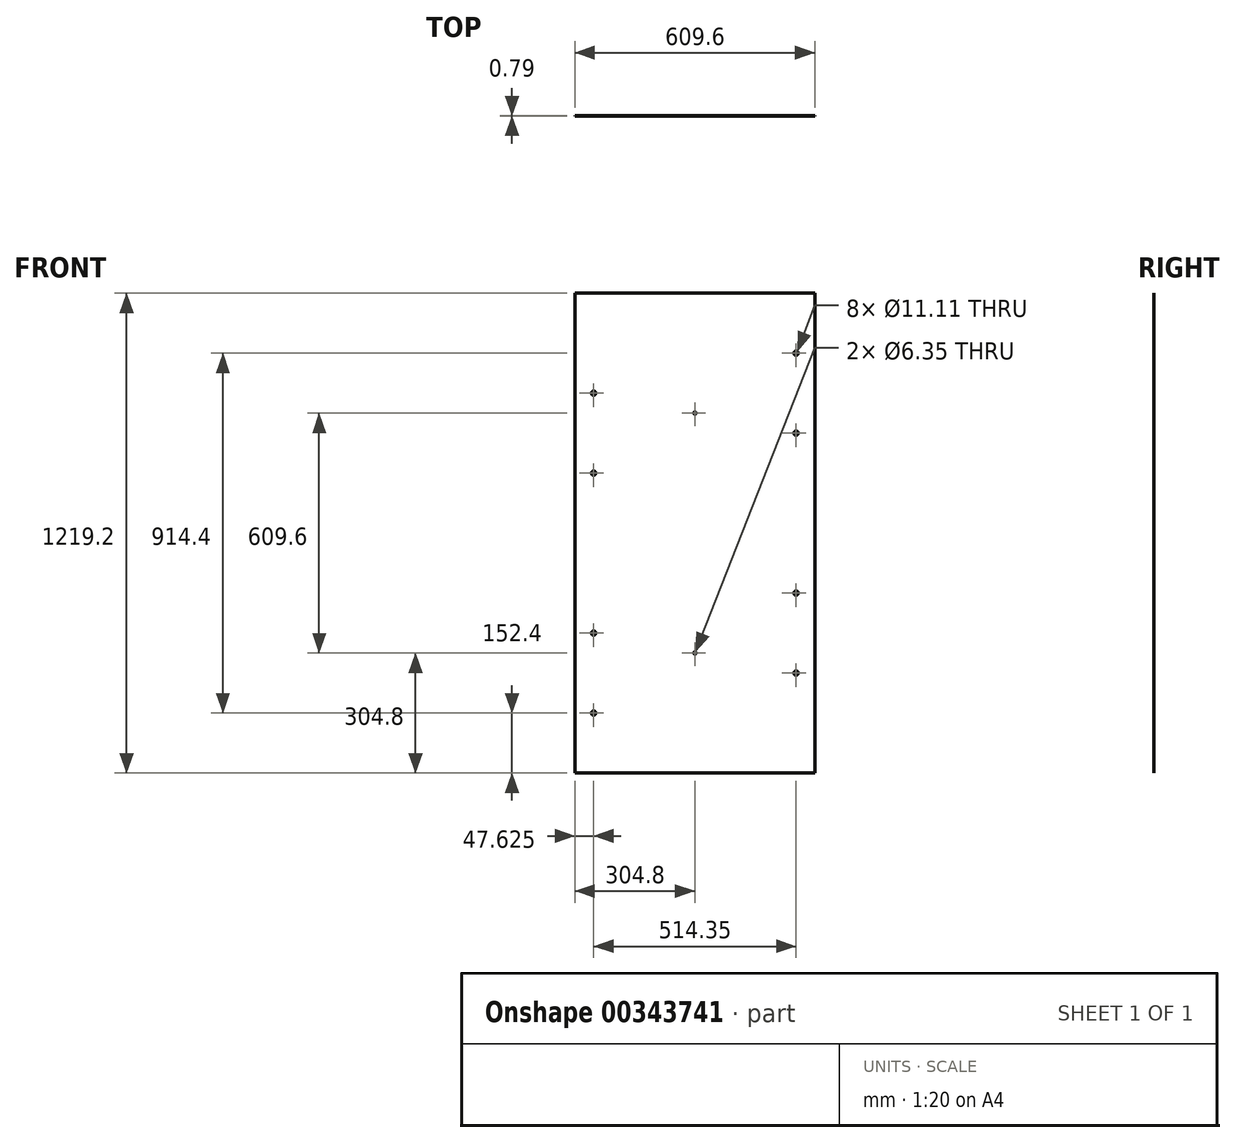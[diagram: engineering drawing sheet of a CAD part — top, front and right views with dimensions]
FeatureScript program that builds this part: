
annotation { "Feature Type Name" : "Feature", "Feature Type Description" : "" }
export const myFeature = defineFeature(function(context is Context, id is Id, definition is map)
    precondition{}
    {
        {
            var Q0;
            Q0=qCreatedBy(makeId("Front.planeOp"),FACE);
            var sketch = newSketch(context, id + "F0", { "sketchPlane" : qUnion([Q0])});
            skLineSegment(sketch, "E0.bottom", {"start": v(0, 0) * mm, "end": v(609.6, 0) * mm});
            skLineSegment(sketch, "E0.top", {"start": v(0, 1219.2) * mm, "end": v(609.6, 1219.2) * mm});
            skLineSegment(sketch, "E0.left", {"start": v(0, 0) * mm, "end": v(0, 1219.2) * mm});
            skLineSegment(sketch, "E0.right", {"start": v(609.6, 0) * mm, "end": v(609.6, 1219.2) * mm});
            skSolve(sketch);
        }
        {
            var Q0;
            Q0=makeQuery(id+"F0.imprint","IMPRINT",FACE,{"disambiguationData":[TD([[makeQuery(id+"F0.imprint","IMPRINT",EDGE,{"derivedFrom":sQuery(id+"F0.wireOp",EDGE,"E0.bottom")}),1.0]])]});
            extrude(context, id + "F1", {"entities" : qUnion([Q0]), "depth" : 0.8 * mm});
        }
        {
            var Q0;
            Q0=makeQuery(id+"F1.opExtrude","CAP_FACE",FACE,{"disambiguationData":[OSD([sQuery(id+"F0.wireOp",EDGE,"E0.bottom"),sQuery(id+"F0.wireOp",EDGE,"E0.top"),sQuery(id+"F0.wireOp",EDGE,"E0.left"),sQuery(id+"F0.wireOp",EDGE,"E0.right")])],"isStart":false});
            var sketch = newSketch(context, id + "F2", { "sketchPlane" : qUnion([Q0])});
            skCircle(sketch, "E1", {"center": v(47.63, 152.4) * mm, "radius": 5.56 * mm});
            skCircle(sketch, "E2", {"center": v(47.63, 355.6) * mm, "radius": 5.56 * mm});
            skCircle(sketch, "E3", {"center": v(561.97, 1066.8) * mm, "radius": 5.56 * mm});
            skCircle(sketch, "E4", {"center": v(561.97, 863.6) * mm, "radius": 5.56 * mm});
            skLineSegment(sketch, "E5", {"start": v(0, 609.6) * mm, "end": v(609.6, 609.6) * mm});
            skCircle(sketch, "E6", {"center": v(47.63, 762) * mm, "radius": 5.56 * mm});
            skCircle(sketch, "E7", {"center": v(47.63, 965.2) * mm, "radius": 5.56 * mm});
            skCircle(sketch, "E8", {"center": v(561.98, 457.2) * mm, "radius": 5.56 * mm});
            skCircle(sketch, "E9", {"center": v(561.98, 254) * mm, "radius": 5.56 * mm});
            skSolve(sketch);
        }
        {
            var Q0;
            Q0=makeQuery(id+"F2.imprint","IMPRINT",FACE,{"disambiguationData":[TD([[makeQuery(id+"F2.imprint","IMPRINT",EDGE,{"derivedFrom":sQuery(id+"F2.wireOp",EDGE,"E2")}),1.0]])]});
            var Q1;
            Q1=makeQuery(id+"F2.imprint","IMPRINT",FACE,{"disambiguationData":[TD([[makeQuery(id+"F2.imprint","IMPRINT",EDGE,{"derivedFrom":sQuery(id+"F2.wireOp",EDGE,"E1")}),1.0]])]});
            var Q2;
            Q2=makeQuery(id+"F2.imprint","IMPRINT",FACE,{"disambiguationData":[TD([[makeQuery(id+"F2.imprint","IMPRINT",EDGE,{"derivedFrom":sQuery(id+"F2.wireOp",EDGE,"E4")}),1.0]])]});
            var Q3;
            Q3=makeQuery(id+"F2.imprint","IMPRINT",FACE,{"disambiguationData":[TD([[makeQuery(id+"F2.imprint","IMPRINT",EDGE,{"derivedFrom":sQuery(id+"F2.wireOp",EDGE,"E3")}),1.0]])]});
            var Q4;
            Q4=makeQuery(id+"F2.imprint","IMPRINT",FACE,{"disambiguationData":[TD([[makeQuery(id+"F2.imprint","IMPRINT",EDGE,{"derivedFrom":sQuery(id+"F2.wireOp",EDGE,"E9")}),1.0]])]});
            var Q5;
            Q5=makeQuery(id+"F2.imprint","IMPRINT",FACE,{"disambiguationData":[TD([[makeQuery(id+"F2.imprint","IMPRINT",EDGE,{"derivedFrom":sQuery(id+"F2.wireOp",EDGE,"E8")}),1.0]])]});
            var Q6;
            Q6=makeQuery(id+"F2.imprint","IMPRINT",FACE,{"disambiguationData":[TD([[makeQuery(id+"F2.imprint","IMPRINT",EDGE,{"derivedFrom":sQuery(id+"F2.wireOp",EDGE,"E7")}),1.0]])]});
            var Q7;
            Q7=makeQuery(id+"F2.imprint","IMPRINT",FACE,{"disambiguationData":[TD([[makeQuery(id+"F2.imprint","IMPRINT",EDGE,{"derivedFrom":sQuery(id+"F2.wireOp",EDGE,"E6")}),1.0]])]});
            extrude(context, id + "F3", {"entities" : qUnion([Q0, Q1, Q2, Q3, Q4, Q5, Q6, Q7]), "operationType" : NewBodyOperationType.REMOVE, "oppositeDirection" : true, "depth" : 25.4 * mm});
        }
        {
            var Q0;
            Q0=makeQuery(id+"F1.opExtrude","CAP_FACE",FACE,{"disambiguationData":[OSD([sQuery(id+"F0.wireOp",EDGE,"E0.bottom"),sQuery(id+"F0.wireOp",EDGE,"E0.top"),sQuery(id+"F0.wireOp",EDGE,"E0.left"),sQuery(id+"F0.wireOp",EDGE,"E0.right")])],"isStart":false});
            var sketch = newSketch(context, id + "F4", { "sketchPlane" : qUnion([Q0])});
            skCircle(sketch, "E10", {"center": v(304.8, 304.8) * mm, "radius": 3.18 * mm});
            skCircle(sketch, "E11", {"center": v(304.8, 914.4) * mm, "radius": 3.18 * mm});
            skSolve(sketch);
        }
        {
            var Q0;
            Q0=makeQuery(id+"F4.imprint","IMPRINT",FACE,{"disambiguationData":[TD([[makeQuery(id+"F4.imprint","IMPRINT",EDGE,{"derivedFrom":sQuery(id+"F4.wireOp",EDGE,"E10")}),1.0]])]});
            var Q1;
            Q1=makeQuery(id+"F4.imprint","IMPRINT",FACE,{"disambiguationData":[TD([[makeQuery(id+"F4.imprint","IMPRINT",EDGE,{"derivedFrom":sQuery(id+"F4.wireOp",EDGE,"E11")}),1.0]])]});
            extrude(context, id + "F5", {"entities" : qUnion([Q0, Q1]), "operationType" : NewBodyOperationType.REMOVE, "oppositeDirection" : true, "depth" : 25.4 * mm});
        }
    });
